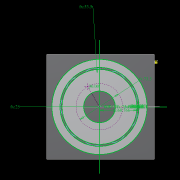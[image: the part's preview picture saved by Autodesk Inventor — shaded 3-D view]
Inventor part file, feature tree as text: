
AUTODESK INVENTOR PART (.ipt)
format: ipt  version: 2022.2 (Build 262287010, 287A)  size: 500,224 bytes
history: native  units: mm
features: other x21, extrude x14, sketch x10, pattern_circular x7, fillet x2, move_body x2, revolve x2, draft x2, plane x1
ambient origin geometry x8: Origin, YZ Plane, XZ Plane, XY Plane, X Axis, Y Axis, Z Axis, Center Point
bodies: Solid5 (feature_tree)
feature tree (61):
  other  "CrossSection1"
  sketch  "Sketch7"  dims[d90=63.418164mm]
  other  "Roller1"
  other  "Roller2"
  sketch  "Sketch22"  dims[d167=8.972256mm]
  sketch  "Sketch2"  dims[d57=4.025mm]
  sketch  "Sketch23"  dims[d173=10.814812mm]
  other  "RevRoller1"
  fillet  "Fillet1"  Radius=60.766033mm
  pattern_circular  "Circular Pattern13"  Count=360  [1 undecoded]
  move_body  "Move Body7"
  revolve  "Revolution13"  [1 undecoded]
  fillet  "Fillet3"  Radius=0.025mm
  pattern_circular  "Circular Pattern14"  [2 undecoded]
  move_body  "Move Body6"
  revolve  "Revolution14"  [1 undecoded]
  other  "OuterRim_Top2"
  other  "OuterRim_Bottom2"
  sketch  "Sketch30"  dims[d201=53.5mm d232=0.0mm d233=3600.0mm]
  plane  "Work Plane7"
  sketch  "Sketch44"  dims[d349=47.579503mm d350=47.550953mm d351=0.025mm d352=0.025mm d354=0.1mm d355=16.135027mm d356=16.163577mm d357=1.0mm d358=90.0deg d359=0.5mm d360=240.0mm d361=360.0deg d363=1.308997mm d367=8.1mm d369=4.014775mm d370=0.1mm d371=1.0mm d372=1.308997mm d373=90.0deg d374=0.5mm d375=240.0mm d376=360.0deg d378=90.0deg d379=0.1mm d380=0.1mm d381=0.1mm d382=0.1mm d383=0.1mm d384=11.191225mm d385=0.0mm d386=0.0mm d391=25.0mm d392=75.0mm d393=1.5mm d394=1.5mm d395=1.5mm d396=1.5mm d397=90.0deg d398=90.0deg d399=90.0deg d400=53.5mm d401=11.191225mm d402=0.0mm d486=0.436332mm d487=0.5mm d488=2.0mm d489=0.0mm d490=20.0mm d495=2.5mm d496=8.0mm d506=13.856406mm d507=55.5mm d508=8.0mm d509=0.05mm d510=2.5mm d511=30.0deg d512=12.0mm d513=6.0mm d514=0.2mm d515=30.0deg d516=131.0mm d517=65.5mm d518=0.2mm d519=100.0mm d520=120.0mm d521=2.0mm d522=150.0mm d530=50.0mm d531=5.5mm d532=5.5mm d533=5.5mm d534=85.75mm d535=73.5mm d536=61.25mm d537=24.5mm d538=3.0mm d539=3.0mm d540=0.0mm d541=0.0mm d542=0.0mm d543=5.0mm d544=3.0mm d545=0.0mm d546=90.0mm d547=360.0deg d549=3.0mm d550=3.0mm d551=2.4mm d552=0.0mm d553=5.595612mm d554=0.0mm d555=2.4mm d556=0.0mm d557=5.595612mm d558=0.0mm d559=5.595612mm d560=0.0mm d561=90.0mm d562=360.0deg d564=60.0mm d565=360.0deg d567=5.0mm d568=5.0mm d569=3.0mm d570=0.0mm d571=5.595612mm d572=0.0mm d573=3.0mm d574=0.0mm d575=5.595612mm d576=0.0mm d577=90.0mm d578=360.0deg d580=60.0mm d581=360.0deg d583=0.436332mm d584=20.0mm d585=8.0mm d587=1.75mm d589=3.0mm d592=2.0mm d593=12.0mm d594=12.0mm d595=0.0mm d596=0.0mm d597=3.0mm d598=12.0mm d599=12.0mm d600=100.0mm d603=30.0deg d604=73.5mm d16=0.872665mm d17=0.872665mm d49=0.872665mm d50=0.872665mm d51=0.872665mm d52=0.872665mm d236=0.5mm d237=0.872665mm d238=0.5mm d239=0.872665mm d282=1.0mm d283=1.0mm d284=1.0mm d285=0.15mm d286=0.25mm d287=0.375mm d288=14.3117mm d289=0.75mm d290=20.594885mm d291=0.0625mm d292=0.75mm d293=0.375mm d405=0.5mm d406=0.872665mm d407=0.5mm d408=0.872665mm d413=0.5mm d414=0.872665mm d415=0.5mm d416=0.872665mm d417=0.5mm d418=0.872665mm d419=0.5mm d420=0.872665mm d421=0.872665mm d431=0.5mm d432=0.872665mm d433=0.5mm d434=0.872665mm d471=0.5mm d472=0.872665mm d473=0.5mm d474=0.872665mm d497=0.5mm d498=0.872665mm d499=0.5mm d500=0.872665mm d590=0.5mm d591=0.872665mm]
  other  "Rotor_"
  draft  "FaceDraft2"
  extrude  "Extrusion9"  Depth=11.191225mm
  other  "Rotor Featurs"
  other  "RotorRim_Bottom"
  extrude  "Extrusion24"  Depth=0.1mm
  extrude  "Extrusion25"  Depth=11.191225mm
  extrude  "Extrusion26"  Depth=11.191225mm
  pattern_circular  "Circular Pattern23"  [2 undecoded]
  sketch  "Sketch41"  dims[d346=0.025mm]
  extrude  "Extrusion27"  TaperAngle=90.0deg  [1 undecoded]
  extrude  "Extrusion28"  Depth=11.191225mm
  extrude  "Extrusion29"  Depth=11.191225mm
  extrude  "Extrusion30"  TaperAngle=360.0deg  [1 undecoded]
  extrude  "Extrusion31"  Depth=11.191225mm
  pattern_circular  "Circular Pattern24"  [2 undecoded]
  pattern_circular  "Circular Pattern25"  [2 undecoded]
  sketch  "Sketch42"  dims[d347=0.1mm]
  extrude  "Extrusion32"  Depth=0.1mm
  extrude  "Extrusion33"  Depth=11.191225mm
  extrude  "Extrusion34"  Depth=11.191225mm
  extrude  "Extrusion35"  TaperAngle=90.0deg  [1 undecoded]
  pattern_circular  "Circular Pattern26"  [2 undecoded]
  pattern_circular  "Circular Pattern27"  Count=24  [1 undecoded]
  draft  "FaceDraft3"
  other  "Cutout"
  extrude  "Extrusion36"  TaperAngle=360.0deg  [1 undecoded]
  other  "2D Equation Curve1"
  sketch  "Sketch40"  dims[d343=16.135027mm d344=16.163577mm d345=0.025mm]
  other  "Work Axis6"
  other  "Work Axis7"
  other  "Work Axis8"
  other  "Work Axis9"
  other  "Work Axis10"
  other  "Work Point1"
  other  "Work Point2"
  other  "Work Point3"
  other  "Work Point4"
  other  "Work Point5"
  sketch  "Sketch43"  dims[d348=0.1mm]
note: 18 required parameter values undecoded (feature->parameter linkage not recoverable at this tier; creation-order binding heuristic only, values carry confidence <= 0.55)